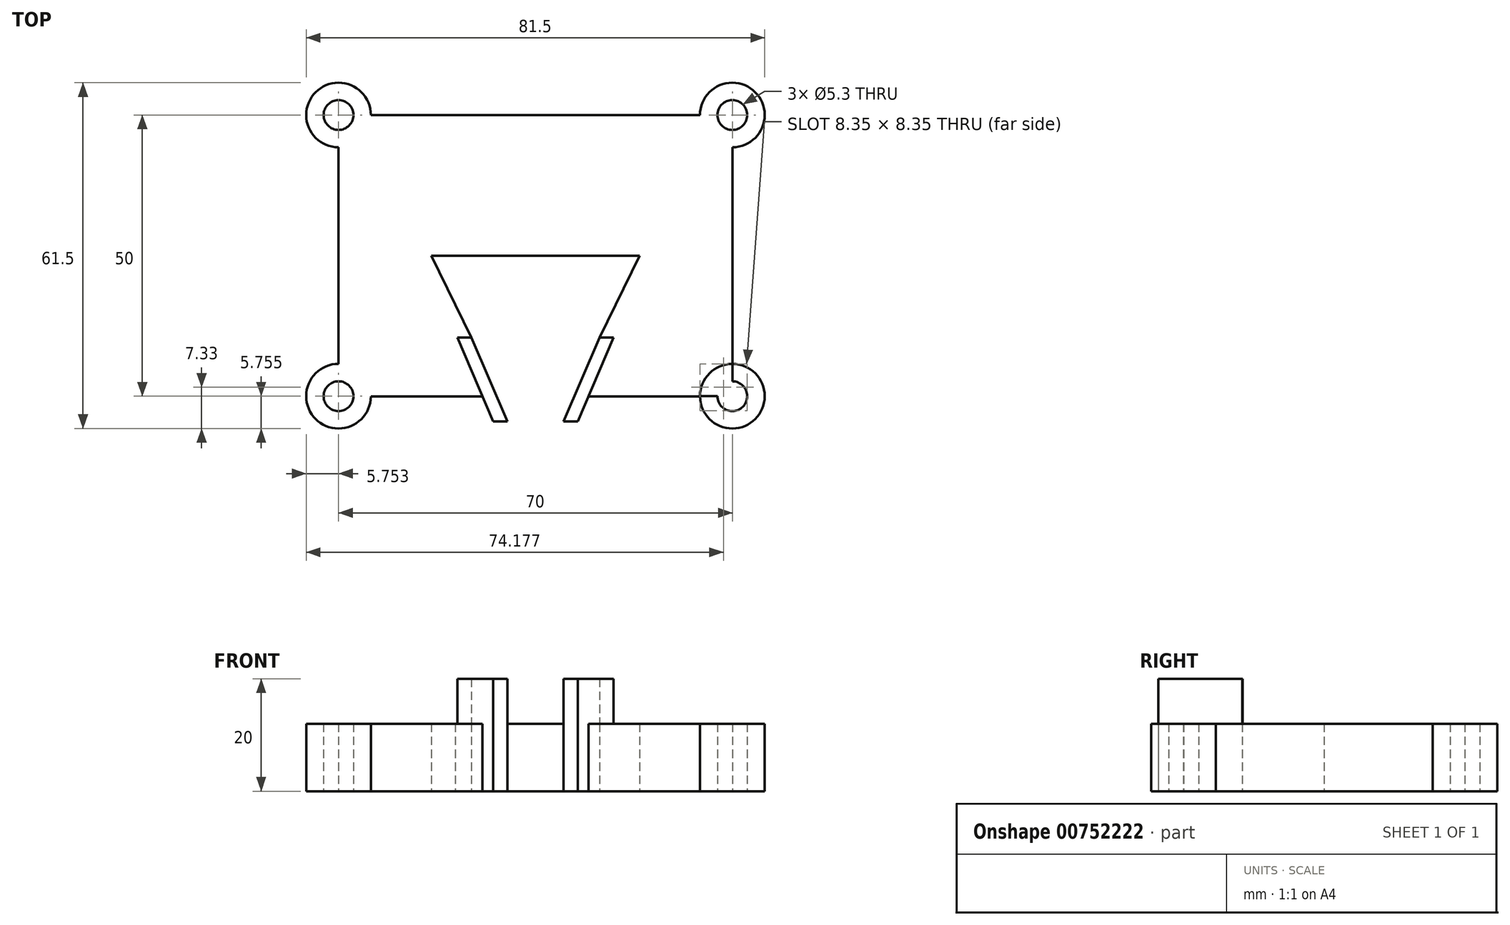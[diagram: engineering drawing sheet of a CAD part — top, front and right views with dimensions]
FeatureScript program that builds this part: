
annotation { "Feature Type Name" : "Feature", "Feature Type Description" : "" }
export const myFeature = defineFeature(function(context is Context, id is Id, definition is map)
    precondition{}
    {
        {
            var Q0;
            Q0=qCreatedBy(makeId("Top.planeOp"),FACE);
            var sketch = newSketch(context, id + "F0", { "sketchPlane" : qUnion([Q0])});
            skLineSegment(sketch, "E0.bottom", {"start": v(-53.17, 40.18) * mm, "end": v(11.53, 40.18) * mm});
            skLineSegment(sketch, "E0.top", {"start": v(-53.17, -9.82) * mm, "end": v(-30.24, -9.82) * mm});
            skLineSegment(sketch, "E0.left", {"start": v(-55.82, 37.53) * mm, "end": v(-55.82, -7.17) * mm});
            skLineSegment(sketch, "E0.right", {"start": v(14.18, 37.53) * mm, "end": v(14.18, -7.17) * mm});
            skCircle(sketch, "E1", {"center": v(14.18, 40.18) * mm, "radius": 2.65 * mm});
            skCircle(sketch, "E2", {"center": v(-55.82, 40.18) * mm, "radius": 2.65 * mm});
            skCircle(sketch, "E3", {"center": v(-55.82, -9.82) * mm, "radius": 2.65 * mm});
            skCircle(sketch, "E4", {"center": v(14.18, -9.82) * mm, "radius": 2.65 * mm});
            skCircle(sketch, "E5", {"center": v(-55.82, 40.18) * mm, "radius": 5.75 * mm});
            skCircle(sketch, "E6", {"center": v(14.18, 40.18) * mm, "radius": 5.75 * mm});
            skCircle(sketch, "E7", {"center": v(14.18, -9.82) * mm, "radius": 5.75 * mm});
            skCircle(sketch, "E8", {"center": v(-55.82, -9.82) * mm, "radius": 5.75 * mm});
            skPoint(sketch, "E9.first.point", {"position": v(-20.82, 40.18) * mm});
            skPoint(sketch, "E9.second.point", {"position": v(-55.82, 15.18) * mm});
            skLineSegment(sketch, "E10.top", {"start": v(-53.17, -9.85) * mm, "end": v(-30.22, -9.85) * mm});
            skLineSegment(sketch, "E10.right", {"start": v(14.2, 37.53) * mm, "end": v(14.2, -7.17) * mm});
            skPoint(sketch, "E10.middle", {"position": v(-20.8, 15.17) * mm});
            skCircle(sketch, "E11", {"center": v(-20.8, 15.17) * mm, "radius": 14.25 * mm});
            skArc(sketch, "E12", {"start": v(-2.3, 15.17) * mm, "mid": v(-20.8, 33.67) * mm, "end": v(-39.3, 15.17) * mm});
            skLineSegment(sketch, "E13", {"start": v(-20.8, -9.82) * mm, "end": v(-20.8, -9.85) * mm});
            skLineSegment(sketch, "E14", {"start": v(-32.2, 0.6) * mm, "end": v(-25.8, -14.34) * mm});
            skLineSegment(sketch, "E15", {"start": v(-15.8, -14.34) * mm, "end": v(-9.41, 0.6) * mm});
            skLineSegment(sketch, "E16", {"start": v(-25.8, -14.34) * mm, "end": v(-28.3, -14.34) * mm});
            skLineSegment(sketch, "E17", {"start": v(-28.3, -14.34) * mm, "end": v(-34.7, 0.64) * mm});
            skLineSegment(sketch, "E18", {"start": v(-34.7, 0.64) * mm, "end": v(-32.2, 0.6) * mm});
            skLineSegment(sketch, "E19", {"start": v(-15.8, -14.34) * mm, "end": v(-13.3, -14.34) * mm});
            skLineSegment(sketch, "E20", {"start": v(-13.3, -14.34) * mm, "end": v(-6.91, 0.6) * mm});
            skLineSegment(sketch, "E21", {"start": v(-6.91, 0.6) * mm, "end": v(-9.41, 0.6) * mm});
            skLineSegment(sketch, "E22.trimOffspring", {"start": v(-55.82, -9.82) * mm, "end": v(-55.82, -9.85) * mm});
            skPoint(sketch, "E23.orphan", {"position": v(14.2, -9.85) * mm});
            skLineSegment(sketch, "E24.trimOffspring", {"start": v(14.18, 40.18) * mm, "end": v(14.2, 40.18) * mm});
            skPoint(sketch, "E25.orphan", {"position": v(-20.8, -14.34) * mm});
            skLineSegment(sketch, "E26.trimOffspring", {"start": v(-11.37, -9.82) * mm, "end": v(11.53, -9.82) * mm});
            skLineSegment(sketch, "E27.trimOffspring", {"start": v(-11.38, -9.85) * mm, "end": v(11.53, -9.85) * mm});
            skLineSegment(sketch, "E28", {"start": v(-20.8, 15.17) * mm, "end": v(-39.3, 15.17) * mm});
            skLineSegment(sketch, "E29", {"start": v(-32.2, 0.6) * mm, "end": v(-39.3, 15.17) * mm});
            skLineSegment(sketch, "E30", {"start": v(-20.8, 15.17) * mm, "end": v(-2.3, 15.17) * mm});
            skLineSegment(sketch, "E31", {"start": v(-9.41, 0.6) * mm, "end": v(-2.3, 15.17) * mm});
            skLineSegment(sketch, "E32", {"start": v(-55.82, 15.18) * mm, "end": v(-20.8, 15.17) * mm});
            skLineSegment(sketch, "E33", {"start": v(-20.8, 15.17) * mm, "end": v(14.2, 15.17) * mm});
            skSolve(sketch);
        }
        {
            var Q0;
            Q0 = qSketchRegion(id + "F0", true);
            extrude(context, id + "F1", {"entities" : qUnion([Q0]), "depth" : 12 * mm, "offsetDistance" : 25 * mm});
        }
        {
            var Q0;
            Q0=makeQuery(id+"F0.imprint","IMPRINT",FACE,{"disambiguationData":[TD([[makeQuery(id+"F0.imprint","IMPRINT",EDGE,{"derivedFrom":sQuery(id+"F0.wireOp",EDGE,"E14")}),-1.0]])]});
            var Q1;
            Q1=makeQuery(id+"F0.imprint","IMPRINT",FACE,{"disambiguationData":[TD([[makeQuery(id+"F0.imprint","IMPRINT",EDGE,{"derivedFrom":sQuery(id+"F0.wireOp",EDGE,"E15")}),-1.0]])]});
            extrude(context, id + "F2", {"entities" : qUnion([Q0, Q1]), "operationType" : NewBodyOperationType.ADD, "depth" : 20 * mm, "offsetDistance" : 25 * mm});
        }
        {
            var Q0;
            {var subQ0=sQuery(id+"F0.wireOp",EDGE,"E28");var subQ1=sQuery(id+"F0.wireOp",EDGE,"E11");var subQ2=makeQuery(id+"F0.imprint","INTERSECT",VERTEX,{"derivedFrom":[subQ1,subQ0]});Q0=makeQuery(id+"F0.imprint","IMPRINT",FACE,{"disambiguationData":[TD([[makeQuery(id+"F0.imprint","IMPRINT",EDGE,{"disambiguationData":[TD([[subQ2,1.0]])],"derivedFrom":subQ1}),1.0]])]});}
            var Q1;
            {var subQ0=sQuery(id+"F0.wireOp",EDGE,"E28");var subQ1=sQuery(id+"F0.wireOp",EDGE,"E11");var subQ2=makeQuery(id+"F0.imprint","INTERSECT",VERTEX,{"derivedFrom":[subQ1,subQ0]});Q1=makeQuery(id+"F0.imprint","IMPRINT",FACE,{"disambiguationData":[TD([[makeQuery(id+"F0.imprint","IMPRINT",EDGE,{"disambiguationData":[TD([[subQ2,-1.0]])],"derivedFrom":subQ1}),1.0]])]});}
            extrude(context, id + "F3", {"entities" : qUnion([Q0, Q1]), "operationType" : NewBodyOperationType.REMOVE, "oppositeDirection" : true, "depth" : -25 * mm, "offsetDistance" : 25 * mm});
        }
    });
